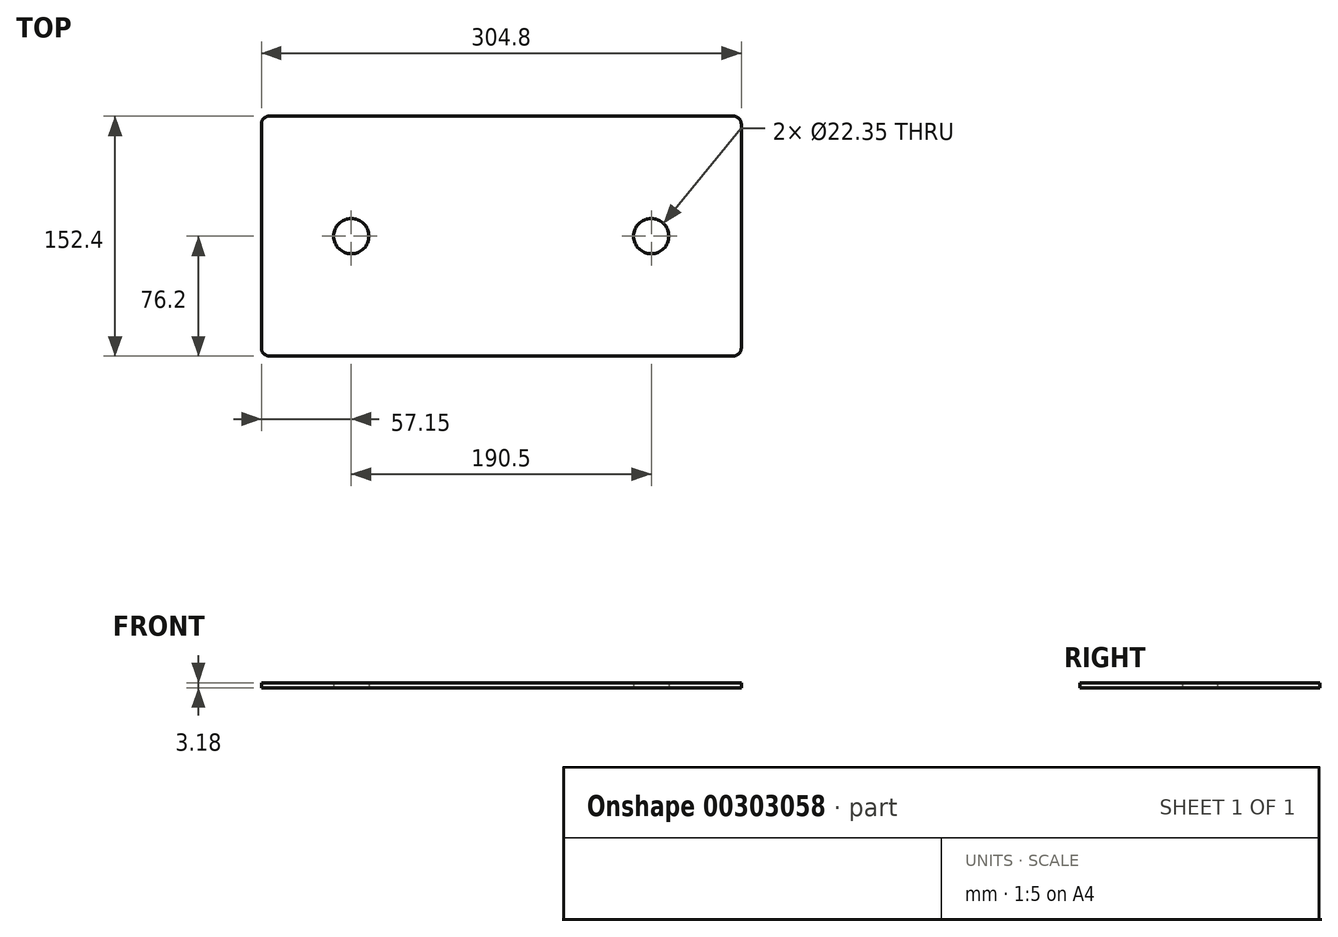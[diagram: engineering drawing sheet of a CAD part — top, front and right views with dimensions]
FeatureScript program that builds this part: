
annotation { "Feature Type Name" : "Feature", "Feature Type Description" : "" }
export const myFeature = defineFeature(function(context is Context, id is Id, definition is map)
    precondition{}
    {
        {
            var Q0;
            Q0=qCreatedBy(makeId("Top.planeOp"),FACE);
            var sketch = newSketch(context, id + "F0", { "sketchPlane" : qUnion([Q0])});
            skLineSegment(sketch, "E0", {"start": v(-152.4, 71.12) * mm, "end": v(-152.4, -71.12) * mm});
            skLineSegment(sketch, "E1", {"start": v(152.4, 71.12) * mm, "end": v(152.4, -71.12) * mm});
            skLineSegment(sketch, "E2", {"start": v(-147.32, 76.2) * mm, "end": v(147.32, 76.2) * mm});
            skLineSegment(sketch, "E3", {"start": v(-147.32, -76.2) * mm, "end": v(147.32, -76.2) * mm});
            skArc(sketch, "E4", {"start": v(-152.4, 71.12) * mm, "mid": v(-150.91, 74.71) * mm, "end": v(-147.32, 76.2) * mm});
            skArc(sketch, "E5.MirrorCS", {"start": v(152.4, 71.12) * mm, "mid": v(150.91, 74.71) * mm, "end": v(147.32, 76.2) * mm});
            skArc(sketch, "E6.MirrorCS", {"start": v(152.4, -71.12) * mm, "mid": v(150.91, -74.71) * mm, "end": v(147.32, -76.2) * mm});
            skArc(sketch, "E7.MirrorCS", {"start": v(-152.4, -71.12) * mm, "mid": v(-150.91, -74.71) * mm, "end": v(-147.32, -76.2) * mm});
            skCircle(sketch, "E8", {"center": v(-95.25, 0) * mm, "radius": 11.18 * mm});
            skCircle(sketch, "E9.MirrorC", {"center": v(95.25, 0) * mm, "radius": 11.18 * mm});
            skSolve(sketch);
        }
        {
            var Q0;
            Q0=makeQuery(id+"F0.imprint","IMPRINT",FACE,{"disambiguationData":[TD([[makeQuery(id+"F0.imprint","IMPRINT",EDGE,{"derivedFrom":sQuery(id+"F0.wireOp",EDGE,"E0")}),1.0]])]});
            extrude(context, id + "F1", {"entities" : qUnion([Q0]), "depth" : 3.17 * mm, "symmetric" : true});
        }
    });
